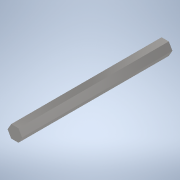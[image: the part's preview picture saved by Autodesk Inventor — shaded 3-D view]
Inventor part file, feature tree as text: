
AUTODESK INVENTOR PART (.ipt)
format: ipt  version: 2020 (Build 240168000, 168)  size: 103,424 bytes
history: native  units: in
note: dims shown in document units (in); Inventor stores cm internally (conversion verified against a paired STEP export)
features: extrude x1, sketch x1
ambient origin geometry x8: Origin, YZ Plane, XZ Plane, XY Plane, X Axis, Y Axis, Z Axis, Center Point
bodies: Solid1 (feature_tree)
feature tree (2):
  extrude  "Extrusion1"  Depth=6.0in TaperAngle=0.0deg
  sketch  "Sketch1"  dims[d0=0.5in d1=6.0in d2=0.0in]
